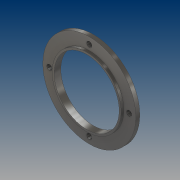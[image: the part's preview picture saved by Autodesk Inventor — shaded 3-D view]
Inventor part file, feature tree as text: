
AUTODESK INVENTOR PART (.ipt)
format: ipt  version: 2021 (Build 250183000, 183)  size: 144,896 bytes
history: native  units: mm
features: extrude x4, thread x4, sketch x4, pattern_circular x1
ambient origin geometry x8: Origin, YZ Plane, XZ Plane, XY Plane, X Axis, Y Axis, Z Axis, Center Point
bodies: Solid1 (feature_tree)
feature tree (13):
  extrude  "Extrusion1"  Depth=3.0mm TaperAngle=0.0deg
  extrude  "Extrusion2"  Depth=49.0mm
  extrude  "Extrusion3"  Depth=2.0mm
  extrude  "Extrusion5"  Depth=10.0mm
  pattern_circular  "Circular Pattern2"  Count=3  [1 undecoded]
  thread  "Thread1"  [1 undecoded]
  thread  "Thread2"  [1 undecoded]
  thread  "Thread3"  [1 undecoded]
  thread  "Thread4"  [1 undecoded]
  sketch  "Sketch1"  dims[d0=70.0mm d1=3.0mm d2=0.0mm]
  sketch  "Sketch2"  dims[d3=52.0mm d4=49.0mm]
  sketch  "Sketch3"  dims[d5=2.0mm d6=0.0mm d7=49.0mm]
  sketch  "Sketch5"  dims[d8=2.0mm d9=0.0mm d17=4.0mm d18=30.0mm d19=2.0mm d20=0.0mm d21=40.0mm d22=360.0deg d24=10.0mm d25=0.0mm d26=10.0mm d27=0.0mm d28=10.0mm d29=0.0mm d30=10.0mm d31=0.0mm]
note: 5 required parameter values undecoded (feature->parameter linkage not recoverable at this tier; creation-order binding heuristic only, values carry confidence <= 0.55)
